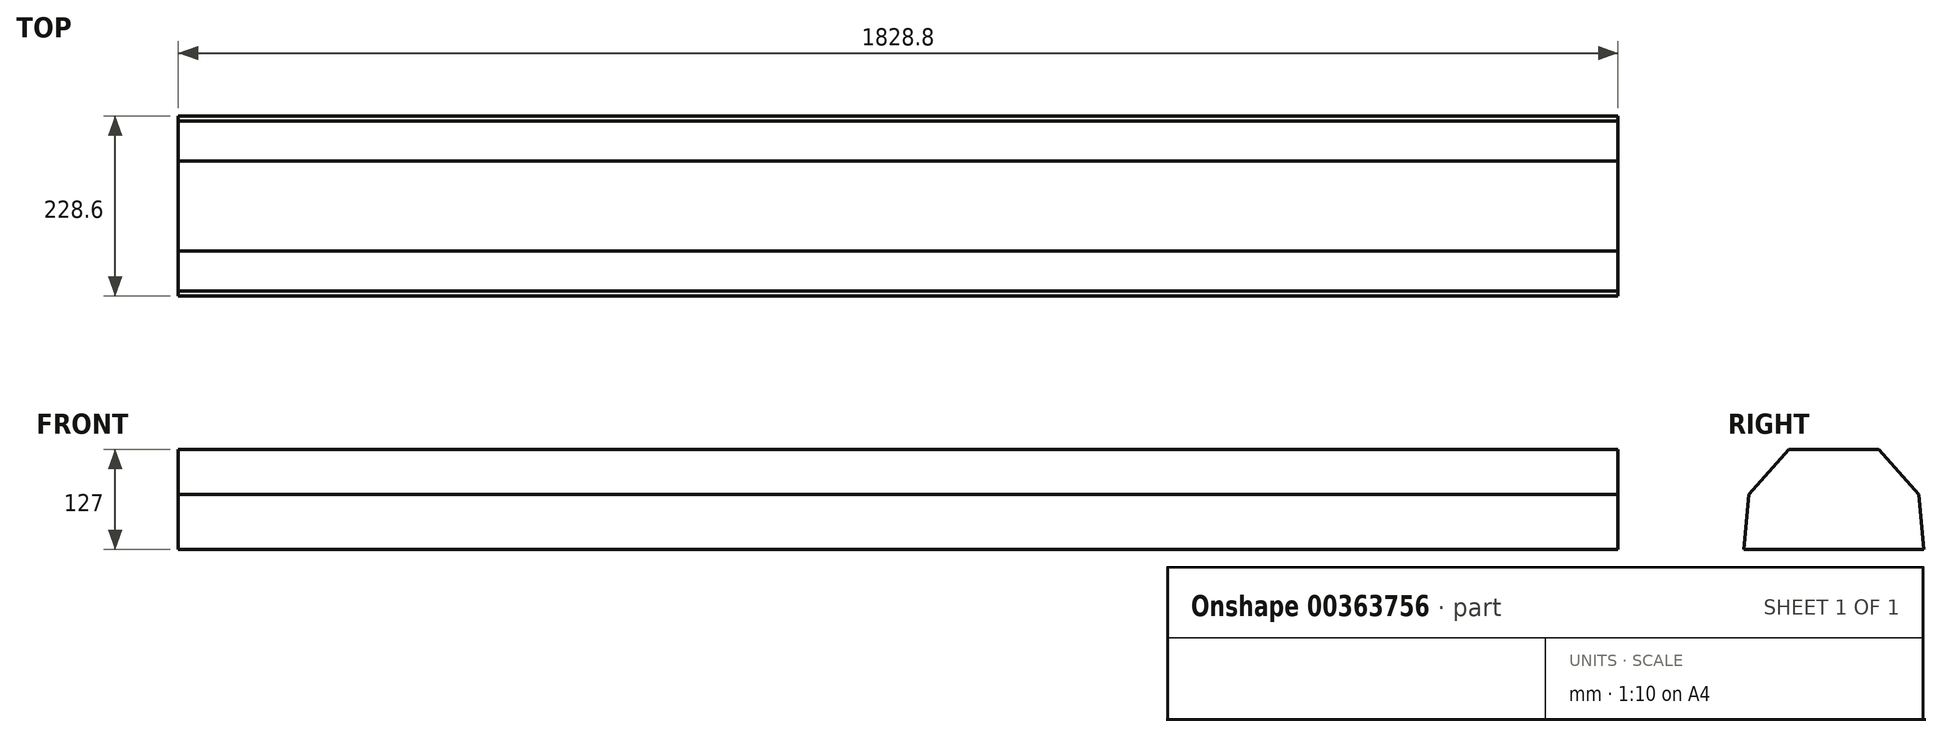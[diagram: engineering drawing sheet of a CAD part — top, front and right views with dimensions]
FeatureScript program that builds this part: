
annotation { "Feature Type Name" : "Feature", "Feature Type Description" : "" }
export const myFeature = defineFeature(function(context is Context, id is Id, definition is map)
    precondition{}
    {
        {
            var Q0;
            Q0=qCreatedBy(makeId("Right.planeOp"),FACE);
            var sketch = newSketch(context, id + "F0", { "sketchPlane" : qUnion([Q0])});
            skLineSegment(sketch, "E0", {"start": v(0, 0) * mm, "end": v(114.3, 0) * mm});
            skLineSegment(sketch, "E1", {"start": v(0, 69.85) * mm, "end": v(107.95, 69.85) * mm, "construction": true});
            skLineSegment(sketch, "E2", {"start": v(0, 127) * mm, "end": v(57.15, 127) * mm});
            skLineSegment(sketch, "E3", {"start": v(114.3, 0) * mm, "end": v(107.95, 69.85) * mm});
            skLineSegment(sketch, "E4", {"start": v(107.95, 69.85) * mm, "end": v(57.15, 127) * mm});
            skLineSegment(sketch, "E5.MirrorCS", {"start": v(0, 127) * mm, "end": v(-57.15, 127) * mm});
            skLineSegment(sketch, "E6.MirrorCS", {"start": v(-107.95, 69.85) * mm, "end": v(-57.15, 127) * mm});
            skLineSegment(sketch, "E7.MirrorCS", {"start": v(-114.3, 0) * mm, "end": v(-107.95, 69.85) * mm});
            skLineSegment(sketch, "E8.MirrorCS", {"start": v(0, 0) * mm, "end": v(-114.3, 0) * mm});
            skSolve(sketch);
        }
        {
            var Q0;
            Q0 = qSketchRegion(id + "F0", true);
            extrude(context, id + "F1", {"entities" : qUnion([Q0]), "depth" : 1828.8 * mm});
        }
    });
